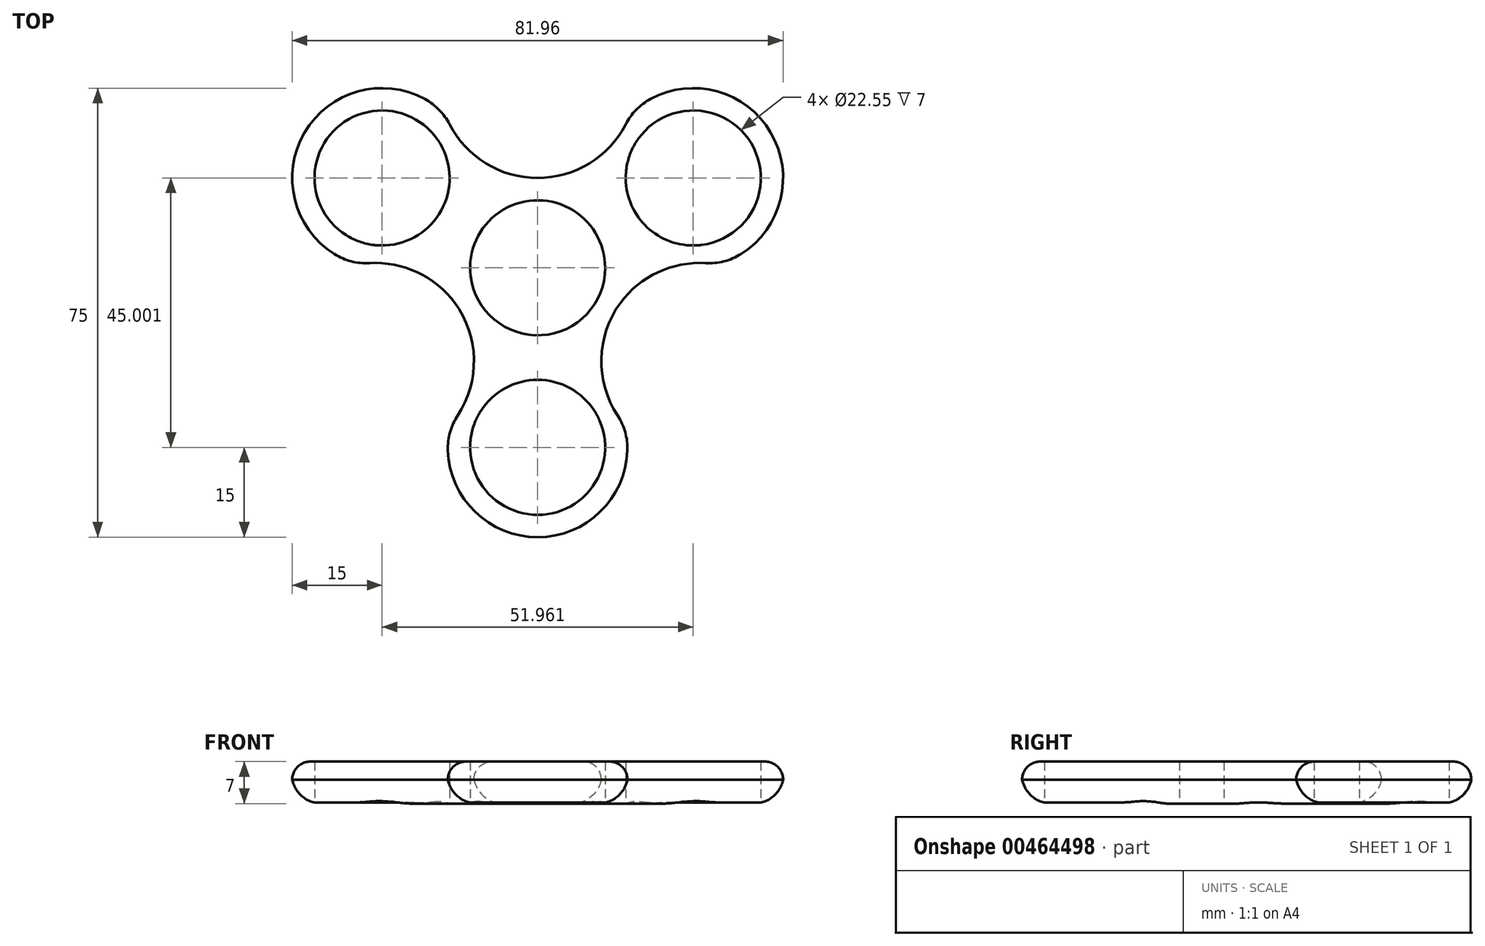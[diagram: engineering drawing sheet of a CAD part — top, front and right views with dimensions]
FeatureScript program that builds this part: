
annotation { "Feature Type Name" : "Feature", "Feature Type Description" : "" }
export const myFeature = defineFeature(function(context is Context, id is Id, definition is map)
    precondition{}
    {
        {
            var Q0;
            Q0=qCreatedBy(makeId("Top.planeOp"),FACE);
            var sketch = newSketch(context, id + "F0", { "sketchPlane" : qUnion([Q0])});
            skCircle(sketch, "E0", {"center": v(0, 0) * mm, "radius": 11.28 * mm});
            skCircle(sketch, "E1", {"center": v(0, 0) * mm, "radius": 15 * mm});
            skCircle(sketch, "E2", {"center": v(0, 0) * mm, "radius": 30 * mm});
            skCircle(sketch, "E3", {"center": v(25.98, 15) * mm, "radius": 15 * mm});
            skCircle(sketch, "E4", {"center": v(-25.98, 15) * mm, "radius": 15 * mm});
            skCircle(sketch, "E5", {"center": v(0, -30) * mm, "radius": 15 * mm});
            skArc(sketch, "E6", {"start": v(-15.47, 25.7) * mm, "mid": v(-9.4, 17.94) * mm, "end": v(0, 15) * mm});
            skArc(sketch, "E7", {"start": v(0, 15) * mm, "mid": v(9.4, 17.94) * mm, "end": v(15.47, 25.7) * mm});
            skArc(sketch, "E8", {"start": v(13.8, -5.88) * mm, "mid": v(10.65, -16.19) * mm, "end": v(14.52, -26.25) * mm});
            skArc(sketch, "E9", {"start": v(30, 0.55) * mm, "mid": v(20.98, -0.36) * mm, "end": v(13.8, -5.88) * mm});
            skArc(sketch, "E10", {"start": v(-13.8, -5.88) * mm, "mid": v(-20.98, -0.36) * mm, "end": v(-30, 0.55) * mm});
            skArc(sketch, "E11", {"start": v(-14.52, -26.25) * mm, "mid": v(-10.65, -16.19) * mm, "end": v(-13.8, -5.88) * mm});
            skCircle(sketch, "E12", {"center": v(-25.98, 15) * mm, "radius": 11.28 * mm});
            skCircle(sketch, "E13", {"center": v(25.98, 15) * mm, "radius": 11.28 * mm});
            skCircle(sketch, "E14", {"center": v(0, -30) * mm, "radius": 11.28 * mm});
            skSolve(sketch);
        }
        {
            var Q0;
            {var subQ1=sQuery(id+"F0.wireOp",EDGE,"E4");var subQ5=makeQuery(id+"F0.imprint","INTERSECT",VERTEX,{"derivedFrom":[sQuery(id+"F0.wireOp",EDGE,"E1"),subQ1]});Q0=makeQuery(id+"F0.imprint","IMPRINT",FACE,{"disambiguationData":[TD([[makeQuery(id+"F0.imprint","IMPRINT",EDGE,{"disambiguationData":[TD([[subQ5,1.0]])],"derivedFrom":subQ1}),1.0]])]});}
            var Q1;
            {var subQ0=sQuery(id+"F0.wireOp",EDGE,"E4");var subQ1=sQuery(id+"F0.wireOp",EDGE,"E2");var subQ2=makeQuery(id+"F0.imprint","INTERSECT",VERTEX,{"derivedFrom":[subQ1,subQ0,sQuery(id+"F0.wireOp",EDGE,"E6")]});Q1=makeQuery(id+"F0.imprint","IMPRINT",FACE,{"disambiguationData":[TD([[makeQuery(id+"F0.imprint","IMPRINT",EDGE,{"disambiguationData":[TD([[subQ2,-1.0]])],"derivedFrom":subQ1}),-1.0]])]});}
            var Q2;
            {var subQ1=sQuery(id+"F0.wireOp",EDGE,"E1");var subQ3=sQuery(id+"F0.wireOp",EDGE,"E4");var subQ4=makeQuery(id+"F0.imprint","INTERSECT",VERTEX,{"derivedFrom":[subQ1,subQ3]});Q2=makeQuery(id+"F0.imprint","IMPRINT",FACE,{"disambiguationData":[TD([[makeQuery(id+"F0.imprint","IMPRINT",EDGE,{"disambiguationData":[TD([[subQ4,-1.0]])],"derivedFrom":subQ3}),-1.0]])]});}
            var Q3;
            Q3=makeQuery(id+"F0.imprint","IMPRINT",FACE,{"disambiguationData":[TD([[makeQuery(id+"F0.imprint","IMPRINT",EDGE,{"derivedFrom":sQuery(id+"F0.wireOp",EDGE,"E0")}),-1.0]])]});
            var Q4;
            {var subQ1=sQuery(id+"F0.wireOp",EDGE,"E1");var subQ3=sQuery(id+"F0.wireOp",EDGE,"E3");var subQ4=makeQuery(id+"F0.imprint","INTERSECT",VERTEX,{"derivedFrom":[subQ1,subQ3]});Q4=makeQuery(id+"F0.imprint","IMPRINT",FACE,{"disambiguationData":[TD([[makeQuery(id+"F0.imprint","IMPRINT",EDGE,{"disambiguationData":[TD([[subQ4,1.0]])],"derivedFrom":subQ3}),-1.0]])]});}
            var Q5;
            {var subQ1=sQuery(id+"F0.wireOp",EDGE,"E3");var subQ5=makeQuery(id+"F0.imprint","INTERSECT",VERTEX,{"derivedFrom":[sQuery(id+"F0.wireOp",EDGE,"E1"),subQ1]});Q5=makeQuery(id+"F0.imprint","IMPRINT",FACE,{"disambiguationData":[TD([[makeQuery(id+"F0.imprint","IMPRINT",EDGE,{"disambiguationData":[TD([[subQ5,1.0]])],"derivedFrom":subQ1}),1.0]])]});}
            var Q6;
            {var subQ0=sQuery(id+"F0.wireOp",EDGE,"E3");var subQ1=sQuery(id+"F0.wireOp",EDGE,"E2");var subQ2=makeQuery(id+"F0.imprint","INTERSECT",VERTEX,{"derivedFrom":[subQ1,subQ0,sQuery(id+"F0.wireOp",EDGE,"E7")]});Q6=makeQuery(id+"F0.imprint","IMPRINT",FACE,{"disambiguationData":[TD([[makeQuery(id+"F0.imprint","IMPRINT",EDGE,{"disambiguationData":[TD([[subQ2,1.0]])],"derivedFrom":subQ1}),-1.0]])]});}
            var Q7;
            {var subQ1=sQuery(id+"F0.wireOp",EDGE,"E1");var subQ3=sQuery(id+"F0.wireOp",EDGE,"E3");var subQ4=makeQuery(id+"F0.imprint","INTERSECT",VERTEX,{"derivedFrom":[subQ1,subQ3]});Q7=makeQuery(id+"F0.imprint","IMPRINT",FACE,{"disambiguationData":[TD([[makeQuery(id+"F0.imprint","IMPRINT",EDGE,{"disambiguationData":[TD([[subQ4,-1.0]])],"derivedFrom":subQ3}),-1.0]])]});}
            var Q8;
            {var subQ0=sQuery(id+"F0.wireOp",EDGE,"E5");var subQ1=sQuery(id+"F0.wireOp",EDGE,"E1");var subQ2=makeQuery(id+"F0.imprint","INTERSECT",VERTEX,{"derivedFrom":[subQ1,subQ0]});Q8=makeQuery(id+"F0.imprint","IMPRINT",FACE,{"disambiguationData":[TD([[makeQuery(id+"F0.imprint","IMPRINT",EDGE,{"disambiguationData":[TD([[subQ2,-1.0]])],"derivedFrom":subQ1}),-1.0]])]});}
            var Q9;
            {var subQ0=sQuery(id+"F0.wireOp",EDGE,"E5");var subQ1=makeQuery(id+"F0.imprint","INTERSECT",VERTEX,{"derivedFrom":[sQuery(id+"F0.wireOp",EDGE,"E1"),subQ0]});Q9=makeQuery(id+"F0.imprint","IMPRINT",FACE,{"disambiguationData":[TD([[makeQuery(id+"F0.imprint","IMPRINT",EDGE,{"disambiguationData":[TD([[subQ1,1.0]])],"derivedFrom":subQ0}),1.0]])]});}
            var Q10;
            {var subQ0=sQuery(id+"F0.wireOp",EDGE,"E11");var subQ1=sQuery(id+"F0.wireOp",EDGE,"E1");var subQ2=makeQuery(id+"F0.imprint","INTERSECT",VERTEX,{"derivedFrom":[subQ1,subQ0]});Q10=makeQuery(id+"F0.imprint","IMPRINT",FACE,{"disambiguationData":[TD([[makeQuery(id+"F0.imprint","IMPRINT",EDGE,{"disambiguationData":[TD([[subQ2,-1.0]])],"derivedFrom":subQ1}),-1.0]])]});}
            var Q11;
            {var subQ0=sQuery(id+"F0.wireOp",EDGE,"E5");var subQ1=sQuery(id+"F0.wireOp",EDGE,"E2");var subQ2=makeQuery(id+"F0.imprint","INTERSECT",VERTEX,{"derivedFrom":[subQ1,subQ0,sQuery(id+"F0.wireOp",EDGE,"E8")]});Q11=makeQuery(id+"F0.imprint","IMPRINT",FACE,{"disambiguationData":[TD([[makeQuery(id+"F0.imprint","IMPRINT",EDGE,{"disambiguationData":[TD([[subQ2,1.0]])],"derivedFrom":subQ1}),-1.0]])]});}
            var Q12;
            {var subQ1=sQuery(id+"F0.wireOp",EDGE,"E1");var subQ3=sQuery(id+"F0.wireOp",EDGE,"E4");var subQ4=makeQuery(id+"F0.imprint","INTERSECT",VERTEX,{"derivedFrom":[subQ1,subQ3]});Q12=makeQuery(id+"F0.imprint","IMPRINT",FACE,{"disambiguationData":[TD([[makeQuery(id+"F0.imprint","IMPRINT",EDGE,{"disambiguationData":[TD([[subQ4,1.0]])],"derivedFrom":subQ3}),-1.0]])]});}
            extrude(context, id + "F1", {"entities" : qUnion([Q0, Q1, Q2, Q3, Q4, Q5, Q6, Q7, Q8, Q9, Q10, Q11, Q12]), "depth" : 7 * mm});
        }
        {
            var Q0;
            Q0=makeQuery(id+"F1.opExtrude","SWEPT_EDGE",EDGE,{"disambiguationData":[OSD([sQuery(id+"F0.wireOp",EDGE,"E2"),sQuery(id+"F0.wireOp",EDGE,"E4"),sQuery(id+"F0.wireOp",EDGE,"E10")])]});
            var Q1;
            Q1=makeQuery(id+"F1.opExtrude","SWEPT_EDGE",EDGE,{"disambiguationData":[OSD([sQuery(id+"F0.wireOp",EDGE,"E2"),sQuery(id+"F0.wireOp",EDGE,"E4"),sQuery(id+"F0.wireOp",EDGE,"E6")])]});
            var Q2;
            Q2=makeQuery(id+"F1.opExtrude","SWEPT_EDGE",EDGE,{"disambiguationData":[OSD([sQuery(id+"F0.wireOp",EDGE,"E2"),sQuery(id+"F0.wireOp",EDGE,"E3"),sQuery(id+"F0.wireOp",EDGE,"E7")])]});
            var Q3;
            Q3=makeQuery(id+"F1.opExtrude","SWEPT_EDGE",EDGE,{"disambiguationData":[OSD([sQuery(id+"F0.wireOp",EDGE,"E2"),sQuery(id+"F0.wireOp",EDGE,"E3"),sQuery(id+"F0.wireOp",EDGE,"E9")])]});
            var Q4;
            Q4=makeQuery(id+"F1.opExtrude","SWEPT_EDGE",EDGE,{"disambiguationData":[OSD([sQuery(id+"F0.wireOp",EDGE,"E2"),sQuery(id+"F0.wireOp",EDGE,"E5"),sQuery(id+"F0.wireOp",EDGE,"E8")])]});
            var Q5;
            Q5=makeQuery(id+"F1.opExtrude","SWEPT_EDGE",EDGE,{"disambiguationData":[OSD([sQuery(id+"F0.wireOp",EDGE,"E2"),sQuery(id+"F0.wireOp",EDGE,"E5"),sQuery(id+"F0.wireOp",EDGE,"E11")])]});
            fillet(context, id + "F2", {"entities" : qUnion([Q0, Q1, Q2, Q3, Q4, Q5]), "radius" : 10 * mm, "tangentPropagation" : true, "allowEdgeOverflow" : false});
        }
        {
            var Q0;
            Q0=makeQuery(id+"F1.opExtrude","CAP_EDGE",EDGE,{"disambiguationData":[OSD([sQuery(id+"F0.wireOp",EDGE,"E10")])],"isStart":false});
            var Q1;
            Q1=makeQuery(id+"F1.opExtrude","CAP_EDGE",EDGE,{"disambiguationData":[OSD([sQuery(id+"F0.wireOp",EDGE,"E11")])],"isStart":false});
            var Q2;
            Q2=makeQuery(id+"F1.opExtrude","CAP_EDGE",EDGE,{"disambiguationData":[OSD([sQuery(id+"F0.wireOp",EDGE,"E5")])],"isStart":false});
            var Q3;
            {var subQ0=sQuery(id+"F0.wireOp",EDGE,"E11");var subQ1=sQuery(id+"F0.wireOp",EDGE,"E5");Q3=makeQuery(id+"F2.opFillet","BLEND_EDGE",EDGE,{"blendedFrom":[makeQuery(id+"F1.opExtrude","SWEPT_EDGE",EDGE,{"disambiguationData":[OSD([sQuery(id+"F0.wireOp",EDGE,"E2"),subQ1,subQ0])]}),makeQuery(id+"F1.opExtrude","CAP_FACE",FACE,{"disambiguationData":[OSD([sQuery(id+"F0.wireOp",EDGE,"E0"),sQuery(id+"F0.wireOp",EDGE,"E3"),sQuery(id+"F0.wireOp",EDGE,"E4"),subQ1,sQuery(id+"F0.wireOp",EDGE,"E6"),sQuery(id+"F0.wireOp",EDGE,"E7"),sQuery(id+"F0.wireOp",EDGE,"E8"),sQuery(id+"F0.wireOp",EDGE,"E9"),sQuery(id+"F0.wireOp",EDGE,"E10"),subQ0,sQuery(id+"F0.wireOp",EDGE,"E12"),sQuery(id+"F0.wireOp",EDGE,"E13"),sQuery(id+"F0.wireOp",EDGE,"E14")])],"isStart":false})],"blendedInto":[makeQuery(id+"F1.opExtrude","CAP_FACE",FACE,{"disambiguationData":[OSD([sQuery(id+"F0.wireOp",EDGE,"E0"),sQuery(id+"F0.wireOp",EDGE,"E3"),sQuery(id+"F0.wireOp",EDGE,"E4"),subQ1,sQuery(id+"F0.wireOp",EDGE,"E6"),sQuery(id+"F0.wireOp",EDGE,"E7"),sQuery(id+"F0.wireOp",EDGE,"E8"),sQuery(id+"F0.wireOp",EDGE,"E9"),sQuery(id+"F0.wireOp",EDGE,"E10"),subQ0,sQuery(id+"F0.wireOp",EDGE,"E12"),sQuery(id+"F0.wireOp",EDGE,"E13"),sQuery(id+"F0.wireOp",EDGE,"E14")])],"isStart":false})]});}
            var Q4;
            {var subQ0=sQuery(id+"F0.wireOp",EDGE,"E8");var subQ1=sQuery(id+"F0.wireOp",EDGE,"E5");Q4=makeQuery(id+"F2.opFillet","BLEND_EDGE",EDGE,{"blendedFrom":[makeQuery(id+"F1.opExtrude","SWEPT_EDGE",EDGE,{"disambiguationData":[OSD([sQuery(id+"F0.wireOp",EDGE,"E2"),subQ1,subQ0])]}),makeQuery(id+"F1.opExtrude","CAP_FACE",FACE,{"disambiguationData":[OSD([sQuery(id+"F0.wireOp",EDGE,"E0"),sQuery(id+"F0.wireOp",EDGE,"E3"),sQuery(id+"F0.wireOp",EDGE,"E4"),subQ1,sQuery(id+"F0.wireOp",EDGE,"E6"),sQuery(id+"F0.wireOp",EDGE,"E7"),subQ0,sQuery(id+"F0.wireOp",EDGE,"E9"),sQuery(id+"F0.wireOp",EDGE,"E10"),sQuery(id+"F0.wireOp",EDGE,"E11"),sQuery(id+"F0.wireOp",EDGE,"E12"),sQuery(id+"F0.wireOp",EDGE,"E13"),sQuery(id+"F0.wireOp",EDGE,"E14")])],"isStart":false})],"blendedInto":[makeQuery(id+"F1.opExtrude","CAP_FACE",FACE,{"disambiguationData":[OSD([sQuery(id+"F0.wireOp",EDGE,"E0"),sQuery(id+"F0.wireOp",EDGE,"E3"),sQuery(id+"F0.wireOp",EDGE,"E4"),subQ1,sQuery(id+"F0.wireOp",EDGE,"E6"),sQuery(id+"F0.wireOp",EDGE,"E7"),subQ0,sQuery(id+"F0.wireOp",EDGE,"E9"),sQuery(id+"F0.wireOp",EDGE,"E10"),sQuery(id+"F0.wireOp",EDGE,"E11"),sQuery(id+"F0.wireOp",EDGE,"E12"),sQuery(id+"F0.wireOp",EDGE,"E13"),sQuery(id+"F0.wireOp",EDGE,"E14")])],"isStart":false})]});}
            var Q5;
            Q5=makeQuery(id+"F1.opExtrude","CAP_EDGE",EDGE,{"disambiguationData":[OSD([sQuery(id+"F0.wireOp",EDGE,"E8")])],"isStart":false});
            var Q6;
            Q6=makeQuery(id+"F1.opExtrude","CAP_EDGE",EDGE,{"disambiguationData":[OSD([sQuery(id+"F0.wireOp",EDGE,"E9")])],"isStart":false});
            var Q7;
            {var subQ0=sQuery(id+"F0.wireOp",EDGE,"E9");var subQ1=sQuery(id+"F0.wireOp",EDGE,"E3");Q7=makeQuery(id+"F2.opFillet","BLEND_EDGE",EDGE,{"blendedFrom":[makeQuery(id+"F1.opExtrude","SWEPT_EDGE",EDGE,{"disambiguationData":[OSD([sQuery(id+"F0.wireOp",EDGE,"E2"),subQ1,subQ0])]}),makeQuery(id+"F1.opExtrude","CAP_FACE",FACE,{"disambiguationData":[OSD([sQuery(id+"F0.wireOp",EDGE,"E0"),subQ1,sQuery(id+"F0.wireOp",EDGE,"E4"),sQuery(id+"F0.wireOp",EDGE,"E5"),sQuery(id+"F0.wireOp",EDGE,"E6"),sQuery(id+"F0.wireOp",EDGE,"E7"),sQuery(id+"F0.wireOp",EDGE,"E8"),subQ0,sQuery(id+"F0.wireOp",EDGE,"E10"),sQuery(id+"F0.wireOp",EDGE,"E11"),sQuery(id+"F0.wireOp",EDGE,"E12"),sQuery(id+"F0.wireOp",EDGE,"E13"),sQuery(id+"F0.wireOp",EDGE,"E14")])],"isStart":false})],"blendedInto":[makeQuery(id+"F1.opExtrude","CAP_FACE",FACE,{"disambiguationData":[OSD([sQuery(id+"F0.wireOp",EDGE,"E0"),subQ1,sQuery(id+"F0.wireOp",EDGE,"E4"),sQuery(id+"F0.wireOp",EDGE,"E5"),sQuery(id+"F0.wireOp",EDGE,"E6"),sQuery(id+"F0.wireOp",EDGE,"E7"),sQuery(id+"F0.wireOp",EDGE,"E8"),subQ0,sQuery(id+"F0.wireOp",EDGE,"E10"),sQuery(id+"F0.wireOp",EDGE,"E11"),sQuery(id+"F0.wireOp",EDGE,"E12"),sQuery(id+"F0.wireOp",EDGE,"E13"),sQuery(id+"F0.wireOp",EDGE,"E14")])],"isStart":false})]});}
            var Q8;
            Q8=makeQuery(id+"F1.opExtrude","CAP_EDGE",EDGE,{"disambiguationData":[OSD([sQuery(id+"F0.wireOp",EDGE,"E3")])],"isStart":false});
            var Q9;
            {var subQ0=sQuery(id+"F0.wireOp",EDGE,"E7");var subQ1=sQuery(id+"F0.wireOp",EDGE,"E3");Q9=makeQuery(id+"F2.opFillet","BLEND_EDGE",EDGE,{"blendedFrom":[makeQuery(id+"F1.opExtrude","SWEPT_EDGE",EDGE,{"disambiguationData":[OSD([sQuery(id+"F0.wireOp",EDGE,"E2"),subQ1,subQ0])]}),makeQuery(id+"F1.opExtrude","CAP_FACE",FACE,{"disambiguationData":[OSD([sQuery(id+"F0.wireOp",EDGE,"E0"),subQ1,sQuery(id+"F0.wireOp",EDGE,"E4"),sQuery(id+"F0.wireOp",EDGE,"E5"),sQuery(id+"F0.wireOp",EDGE,"E6"),subQ0,sQuery(id+"F0.wireOp",EDGE,"E8"),sQuery(id+"F0.wireOp",EDGE,"E9"),sQuery(id+"F0.wireOp",EDGE,"E10"),sQuery(id+"F0.wireOp",EDGE,"E11"),sQuery(id+"F0.wireOp",EDGE,"E12"),sQuery(id+"F0.wireOp",EDGE,"E13"),sQuery(id+"F0.wireOp",EDGE,"E14")])],"isStart":false})],"blendedInto":[makeQuery(id+"F1.opExtrude","CAP_FACE",FACE,{"disambiguationData":[OSD([sQuery(id+"F0.wireOp",EDGE,"E0"),subQ1,sQuery(id+"F0.wireOp",EDGE,"E4"),sQuery(id+"F0.wireOp",EDGE,"E5"),sQuery(id+"F0.wireOp",EDGE,"E6"),subQ0,sQuery(id+"F0.wireOp",EDGE,"E8"),sQuery(id+"F0.wireOp",EDGE,"E9"),sQuery(id+"F0.wireOp",EDGE,"E10"),sQuery(id+"F0.wireOp",EDGE,"E11"),sQuery(id+"F0.wireOp",EDGE,"E12"),sQuery(id+"F0.wireOp",EDGE,"E13"),sQuery(id+"F0.wireOp",EDGE,"E14")])],"isStart":false})]});}
            var Q10;
            Q10=makeQuery(id+"F1.opExtrude","CAP_EDGE",EDGE,{"disambiguationData":[OSD([sQuery(id+"F0.wireOp",EDGE,"E6"),sQuery(id+"F0.wireOp",EDGE,"E7")])],"isStart":false});
            var Q11;
            {var subQ0=sQuery(id+"F0.wireOp",EDGE,"E6");var subQ1=sQuery(id+"F0.wireOp",EDGE,"E4");Q11=makeQuery(id+"F2.opFillet","BLEND_EDGE",EDGE,{"blendedFrom":[makeQuery(id+"F1.opExtrude","SWEPT_EDGE",EDGE,{"disambiguationData":[OSD([sQuery(id+"F0.wireOp",EDGE,"E2"),subQ1,subQ0])]}),makeQuery(id+"F1.opExtrude","CAP_FACE",FACE,{"disambiguationData":[OSD([sQuery(id+"F0.wireOp",EDGE,"E0"),sQuery(id+"F0.wireOp",EDGE,"E3"),subQ1,sQuery(id+"F0.wireOp",EDGE,"E5"),subQ0,sQuery(id+"F0.wireOp",EDGE,"E7"),sQuery(id+"F0.wireOp",EDGE,"E8"),sQuery(id+"F0.wireOp",EDGE,"E9"),sQuery(id+"F0.wireOp",EDGE,"E10"),sQuery(id+"F0.wireOp",EDGE,"E11"),sQuery(id+"F0.wireOp",EDGE,"E12"),sQuery(id+"F0.wireOp",EDGE,"E13"),sQuery(id+"F0.wireOp",EDGE,"E14")])],"isStart":false})],"blendedInto":[makeQuery(id+"F1.opExtrude","CAP_FACE",FACE,{"disambiguationData":[OSD([sQuery(id+"F0.wireOp",EDGE,"E0"),sQuery(id+"F0.wireOp",EDGE,"E3"),subQ1,sQuery(id+"F0.wireOp",EDGE,"E5"),subQ0,sQuery(id+"F0.wireOp",EDGE,"E7"),sQuery(id+"F0.wireOp",EDGE,"E8"),sQuery(id+"F0.wireOp",EDGE,"E9"),sQuery(id+"F0.wireOp",EDGE,"E10"),sQuery(id+"F0.wireOp",EDGE,"E11"),sQuery(id+"F0.wireOp",EDGE,"E12"),sQuery(id+"F0.wireOp",EDGE,"E13"),sQuery(id+"F0.wireOp",EDGE,"E14")])],"isStart":false})]});}
            var Q12;
            Q12=makeQuery(id+"F1.opExtrude","CAP_EDGE",EDGE,{"disambiguationData":[OSD([sQuery(id+"F0.wireOp",EDGE,"E4")])],"isStart":false});
            var Q13;
            {var subQ0=sQuery(id+"F0.wireOp",EDGE,"E10");var subQ1=sQuery(id+"F0.wireOp",EDGE,"E4");Q13=makeQuery(id+"F2.opFillet","BLEND_EDGE",EDGE,{"blendedFrom":[makeQuery(id+"F1.opExtrude","SWEPT_EDGE",EDGE,{"disambiguationData":[OSD([sQuery(id+"F0.wireOp",EDGE,"E2"),subQ1,subQ0])]}),makeQuery(id+"F1.opExtrude","CAP_FACE",FACE,{"disambiguationData":[OSD([sQuery(id+"F0.wireOp",EDGE,"E0"),sQuery(id+"F0.wireOp",EDGE,"E3"),subQ1,sQuery(id+"F0.wireOp",EDGE,"E5"),sQuery(id+"F0.wireOp",EDGE,"E6"),sQuery(id+"F0.wireOp",EDGE,"E7"),sQuery(id+"F0.wireOp",EDGE,"E8"),sQuery(id+"F0.wireOp",EDGE,"E9"),subQ0,sQuery(id+"F0.wireOp",EDGE,"E11"),sQuery(id+"F0.wireOp",EDGE,"E12"),sQuery(id+"F0.wireOp",EDGE,"E13"),sQuery(id+"F0.wireOp",EDGE,"E14")])],"isStart":false})],"blendedInto":[makeQuery(id+"F1.opExtrude","CAP_FACE",FACE,{"disambiguationData":[OSD([sQuery(id+"F0.wireOp",EDGE,"E0"),sQuery(id+"F0.wireOp",EDGE,"E3"),subQ1,sQuery(id+"F0.wireOp",EDGE,"E5"),sQuery(id+"F0.wireOp",EDGE,"E6"),sQuery(id+"F0.wireOp",EDGE,"E7"),sQuery(id+"F0.wireOp",EDGE,"E8"),sQuery(id+"F0.wireOp",EDGE,"E9"),subQ0,sQuery(id+"F0.wireOp",EDGE,"E11"),sQuery(id+"F0.wireOp",EDGE,"E12"),sQuery(id+"F0.wireOp",EDGE,"E13"),sQuery(id+"F0.wireOp",EDGE,"E14")])],"isStart":false})]});}
            fillet(context, id + "F3", {"entities" : qUnion([Q0, Q1, Q2, Q3, Q4, Q5, Q6, Q7, Q8, Q9, Q10, Q11, Q12, Q13]), "radius" : 3 * mm, "tangentPropagation" : true, "allowEdgeOverflow" : false});
        }
        {
            var Q0;
            Q0=makeQuery(id+"F1.opExtrude","CAP_EDGE",EDGE,{"disambiguationData":[OSD([sQuery(id+"F0.wireOp",EDGE,"E11")])],"isStart":true});
            var Q1;
            {var subQ0=sQuery(id+"F0.wireOp",EDGE,"E11");var subQ1=sQuery(id+"F0.wireOp",EDGE,"E5");Q1=makeQuery(id+"F2.opFillet","BLEND_EDGE",EDGE,{"blendedFrom":[makeQuery(id+"F1.opExtrude","SWEPT_EDGE",EDGE,{"disambiguationData":[OSD([sQuery(id+"F0.wireOp",EDGE,"E2"),subQ1,subQ0])]}),makeQuery(id+"F1.opExtrude","CAP_FACE",FACE,{"disambiguationData":[OSD([sQuery(id+"F0.wireOp",EDGE,"E0"),sQuery(id+"F0.wireOp",EDGE,"E3"),sQuery(id+"F0.wireOp",EDGE,"E4"),subQ1,sQuery(id+"F0.wireOp",EDGE,"E6"),sQuery(id+"F0.wireOp",EDGE,"E7"),sQuery(id+"F0.wireOp",EDGE,"E8"),sQuery(id+"F0.wireOp",EDGE,"E9"),sQuery(id+"F0.wireOp",EDGE,"E10"),subQ0,sQuery(id+"F0.wireOp",EDGE,"E12"),sQuery(id+"F0.wireOp",EDGE,"E13"),sQuery(id+"F0.wireOp",EDGE,"E14")])],"isStart":true})],"blendedInto":[makeQuery(id+"F1.opExtrude","CAP_FACE",FACE,{"disambiguationData":[OSD([sQuery(id+"F0.wireOp",EDGE,"E0"),sQuery(id+"F0.wireOp",EDGE,"E3"),sQuery(id+"F0.wireOp",EDGE,"E4"),subQ1,sQuery(id+"F0.wireOp",EDGE,"E6"),sQuery(id+"F0.wireOp",EDGE,"E7"),sQuery(id+"F0.wireOp",EDGE,"E8"),sQuery(id+"F0.wireOp",EDGE,"E9"),sQuery(id+"F0.wireOp",EDGE,"E10"),subQ0,sQuery(id+"F0.wireOp",EDGE,"E12"),sQuery(id+"F0.wireOp",EDGE,"E13"),sQuery(id+"F0.wireOp",EDGE,"E14")])],"isStart":true})]});}
            var Q2;
            Q2=makeQuery(id+"F1.opExtrude","CAP_EDGE",EDGE,{"disambiguationData":[OSD([sQuery(id+"F0.wireOp",EDGE,"E5")])],"isStart":true});
            var Q3;
            {var subQ0=sQuery(id+"F0.wireOp",EDGE,"E8");var subQ1=sQuery(id+"F0.wireOp",EDGE,"E5");Q3=makeQuery(id+"F2.opFillet","BLEND_EDGE",EDGE,{"blendedFrom":[makeQuery(id+"F1.opExtrude","SWEPT_EDGE",EDGE,{"disambiguationData":[OSD([sQuery(id+"F0.wireOp",EDGE,"E2"),subQ1,subQ0])]}),makeQuery(id+"F1.opExtrude","CAP_FACE",FACE,{"disambiguationData":[OSD([sQuery(id+"F0.wireOp",EDGE,"E0"),sQuery(id+"F0.wireOp",EDGE,"E3"),sQuery(id+"F0.wireOp",EDGE,"E4"),subQ1,sQuery(id+"F0.wireOp",EDGE,"E6"),sQuery(id+"F0.wireOp",EDGE,"E7"),subQ0,sQuery(id+"F0.wireOp",EDGE,"E9"),sQuery(id+"F0.wireOp",EDGE,"E10"),sQuery(id+"F0.wireOp",EDGE,"E11"),sQuery(id+"F0.wireOp",EDGE,"E12"),sQuery(id+"F0.wireOp",EDGE,"E13"),sQuery(id+"F0.wireOp",EDGE,"E14")])],"isStart":true})],"blendedInto":[makeQuery(id+"F1.opExtrude","CAP_FACE",FACE,{"disambiguationData":[OSD([sQuery(id+"F0.wireOp",EDGE,"E0"),sQuery(id+"F0.wireOp",EDGE,"E3"),sQuery(id+"F0.wireOp",EDGE,"E4"),subQ1,sQuery(id+"F0.wireOp",EDGE,"E6"),sQuery(id+"F0.wireOp",EDGE,"E7"),subQ0,sQuery(id+"F0.wireOp",EDGE,"E9"),sQuery(id+"F0.wireOp",EDGE,"E10"),sQuery(id+"F0.wireOp",EDGE,"E11"),sQuery(id+"F0.wireOp",EDGE,"E12"),sQuery(id+"F0.wireOp",EDGE,"E13"),sQuery(id+"F0.wireOp",EDGE,"E14")])],"isStart":true})]});}
            var Q4;
            Q4=makeQuery(id+"F1.opExtrude","CAP_EDGE",EDGE,{"disambiguationData":[OSD([sQuery(id+"F0.wireOp",EDGE,"E8")])],"isStart":true});
            var Q5;
            Q5=makeQuery(id+"F1.opExtrude","CAP_EDGE",EDGE,{"disambiguationData":[OSD([sQuery(id+"F0.wireOp",EDGE,"E9")])],"isStart":true});
            var Q6;
            {var subQ0=sQuery(id+"F0.wireOp",EDGE,"E9");var subQ1=sQuery(id+"F0.wireOp",EDGE,"E3");Q6=makeQuery(id+"F2.opFillet","BLEND_EDGE",EDGE,{"blendedFrom":[makeQuery(id+"F1.opExtrude","SWEPT_EDGE",EDGE,{"disambiguationData":[OSD([sQuery(id+"F0.wireOp",EDGE,"E2"),subQ1,subQ0])]}),makeQuery(id+"F1.opExtrude","CAP_FACE",FACE,{"disambiguationData":[OSD([sQuery(id+"F0.wireOp",EDGE,"E0"),subQ1,sQuery(id+"F0.wireOp",EDGE,"E4"),sQuery(id+"F0.wireOp",EDGE,"E5"),sQuery(id+"F0.wireOp",EDGE,"E6"),sQuery(id+"F0.wireOp",EDGE,"E7"),sQuery(id+"F0.wireOp",EDGE,"E8"),subQ0,sQuery(id+"F0.wireOp",EDGE,"E10"),sQuery(id+"F0.wireOp",EDGE,"E11"),sQuery(id+"F0.wireOp",EDGE,"E12"),sQuery(id+"F0.wireOp",EDGE,"E13"),sQuery(id+"F0.wireOp",EDGE,"E14")])],"isStart":true})],"blendedInto":[makeQuery(id+"F1.opExtrude","CAP_FACE",FACE,{"disambiguationData":[OSD([sQuery(id+"F0.wireOp",EDGE,"E0"),subQ1,sQuery(id+"F0.wireOp",EDGE,"E4"),sQuery(id+"F0.wireOp",EDGE,"E5"),sQuery(id+"F0.wireOp",EDGE,"E6"),sQuery(id+"F0.wireOp",EDGE,"E7"),sQuery(id+"F0.wireOp",EDGE,"E8"),subQ0,sQuery(id+"F0.wireOp",EDGE,"E10"),sQuery(id+"F0.wireOp",EDGE,"E11"),sQuery(id+"F0.wireOp",EDGE,"E12"),sQuery(id+"F0.wireOp",EDGE,"E13"),sQuery(id+"F0.wireOp",EDGE,"E14")])],"isStart":true})]});}
            var Q7;
            Q7=makeQuery(id+"F1.opExtrude","CAP_EDGE",EDGE,{"disambiguationData":[OSD([sQuery(id+"F0.wireOp",EDGE,"E3")])],"isStart":true});
            var Q8;
            {var subQ0=sQuery(id+"F0.wireOp",EDGE,"E7");var subQ1=sQuery(id+"F0.wireOp",EDGE,"E3");Q8=makeQuery(id+"F2.opFillet","BLEND_EDGE",EDGE,{"blendedFrom":[makeQuery(id+"F1.opExtrude","SWEPT_EDGE",EDGE,{"disambiguationData":[OSD([sQuery(id+"F0.wireOp",EDGE,"E2"),subQ1,subQ0])]}),makeQuery(id+"F1.opExtrude","CAP_FACE",FACE,{"disambiguationData":[OSD([sQuery(id+"F0.wireOp",EDGE,"E0"),subQ1,sQuery(id+"F0.wireOp",EDGE,"E4"),sQuery(id+"F0.wireOp",EDGE,"E5"),sQuery(id+"F0.wireOp",EDGE,"E6"),subQ0,sQuery(id+"F0.wireOp",EDGE,"E8"),sQuery(id+"F0.wireOp",EDGE,"E9"),sQuery(id+"F0.wireOp",EDGE,"E10"),sQuery(id+"F0.wireOp",EDGE,"E11"),sQuery(id+"F0.wireOp",EDGE,"E12"),sQuery(id+"F0.wireOp",EDGE,"E13"),sQuery(id+"F0.wireOp",EDGE,"E14")])],"isStart":true})],"blendedInto":[makeQuery(id+"F1.opExtrude","CAP_FACE",FACE,{"disambiguationData":[OSD([sQuery(id+"F0.wireOp",EDGE,"E0"),subQ1,sQuery(id+"F0.wireOp",EDGE,"E4"),sQuery(id+"F0.wireOp",EDGE,"E5"),sQuery(id+"F0.wireOp",EDGE,"E6"),subQ0,sQuery(id+"F0.wireOp",EDGE,"E8"),sQuery(id+"F0.wireOp",EDGE,"E9"),sQuery(id+"F0.wireOp",EDGE,"E10"),sQuery(id+"F0.wireOp",EDGE,"E11"),sQuery(id+"F0.wireOp",EDGE,"E12"),sQuery(id+"F0.wireOp",EDGE,"E13"),sQuery(id+"F0.wireOp",EDGE,"E14")])],"isStart":true})]});}
            var Q9;
            Q9=makeQuery(id+"F1.opExtrude","CAP_EDGE",EDGE,{"disambiguationData":[OSD([sQuery(id+"F0.wireOp",EDGE,"E6"),sQuery(id+"F0.wireOp",EDGE,"E7")])],"isStart":true});
            var Q10;
            {var subQ0=sQuery(id+"F0.wireOp",EDGE,"E6");var subQ1=sQuery(id+"F0.wireOp",EDGE,"E4");Q10=makeQuery(id+"F2.opFillet","BLEND_EDGE",EDGE,{"blendedFrom":[makeQuery(id+"F1.opExtrude","SWEPT_EDGE",EDGE,{"disambiguationData":[OSD([sQuery(id+"F0.wireOp",EDGE,"E2"),subQ1,subQ0])]}),makeQuery(id+"F1.opExtrude","CAP_FACE",FACE,{"disambiguationData":[OSD([sQuery(id+"F0.wireOp",EDGE,"E0"),sQuery(id+"F0.wireOp",EDGE,"E3"),subQ1,sQuery(id+"F0.wireOp",EDGE,"E5"),subQ0,sQuery(id+"F0.wireOp",EDGE,"E7"),sQuery(id+"F0.wireOp",EDGE,"E8"),sQuery(id+"F0.wireOp",EDGE,"E9"),sQuery(id+"F0.wireOp",EDGE,"E10"),sQuery(id+"F0.wireOp",EDGE,"E11"),sQuery(id+"F0.wireOp",EDGE,"E12"),sQuery(id+"F0.wireOp",EDGE,"E13"),sQuery(id+"F0.wireOp",EDGE,"E14")])],"isStart":true})],"blendedInto":[makeQuery(id+"F1.opExtrude","CAP_FACE",FACE,{"disambiguationData":[OSD([sQuery(id+"F0.wireOp",EDGE,"E0"),sQuery(id+"F0.wireOp",EDGE,"E3"),subQ1,sQuery(id+"F0.wireOp",EDGE,"E5"),subQ0,sQuery(id+"F0.wireOp",EDGE,"E7"),sQuery(id+"F0.wireOp",EDGE,"E8"),sQuery(id+"F0.wireOp",EDGE,"E9"),sQuery(id+"F0.wireOp",EDGE,"E10"),sQuery(id+"F0.wireOp",EDGE,"E11"),sQuery(id+"F0.wireOp",EDGE,"E12"),sQuery(id+"F0.wireOp",EDGE,"E13"),sQuery(id+"F0.wireOp",EDGE,"E14")])],"isStart":true})]});}
            var Q11;
            Q11=makeQuery(id+"F1.opExtrude","CAP_EDGE",EDGE,{"disambiguationData":[OSD([sQuery(id+"F0.wireOp",EDGE,"E4")])],"isStart":true});
            var Q12;
            {var subQ0=sQuery(id+"F0.wireOp",EDGE,"E10");var subQ1=sQuery(id+"F0.wireOp",EDGE,"E4");Q12=makeQuery(id+"F2.opFillet","BLEND_EDGE",EDGE,{"blendedFrom":[makeQuery(id+"F1.opExtrude","SWEPT_EDGE",EDGE,{"disambiguationData":[OSD([sQuery(id+"F0.wireOp",EDGE,"E2"),subQ1,subQ0])]}),makeQuery(id+"F1.opExtrude","CAP_FACE",FACE,{"disambiguationData":[OSD([sQuery(id+"F0.wireOp",EDGE,"E0"),sQuery(id+"F0.wireOp",EDGE,"E3"),subQ1,sQuery(id+"F0.wireOp",EDGE,"E5"),sQuery(id+"F0.wireOp",EDGE,"E6"),sQuery(id+"F0.wireOp",EDGE,"E7"),sQuery(id+"F0.wireOp",EDGE,"E8"),sQuery(id+"F0.wireOp",EDGE,"E9"),subQ0,sQuery(id+"F0.wireOp",EDGE,"E11"),sQuery(id+"F0.wireOp",EDGE,"E12"),sQuery(id+"F0.wireOp",EDGE,"E13"),sQuery(id+"F0.wireOp",EDGE,"E14")])],"isStart":true})],"blendedInto":[makeQuery(id+"F1.opExtrude","CAP_FACE",FACE,{"disambiguationData":[OSD([sQuery(id+"F0.wireOp",EDGE,"E0"),sQuery(id+"F0.wireOp",EDGE,"E3"),subQ1,sQuery(id+"F0.wireOp",EDGE,"E5"),sQuery(id+"F0.wireOp",EDGE,"E6"),sQuery(id+"F0.wireOp",EDGE,"E7"),sQuery(id+"F0.wireOp",EDGE,"E8"),sQuery(id+"F0.wireOp",EDGE,"E9"),subQ0,sQuery(id+"F0.wireOp",EDGE,"E11"),sQuery(id+"F0.wireOp",EDGE,"E12"),sQuery(id+"F0.wireOp",EDGE,"E13"),sQuery(id+"F0.wireOp",EDGE,"E14")])],"isStart":true})]});}
            var Q13;
            Q13=makeQuery(id+"F1.opExtrude","CAP_EDGE",EDGE,{"disambiguationData":[OSD([sQuery(id+"F0.wireOp",EDGE,"E10")])],"isStart":true});
            fillet(context, id + "F4", {"entities" : qUnion([Q0, Q1, Q2, Q3, Q4, Q5, Q6, Q7, Q8, Q9, Q10, Q11, Q12, Q13]), "radius" : 5 * mm, "tangentPropagation" : true, "allowEdgeOverflow" : false});
        }
    });
